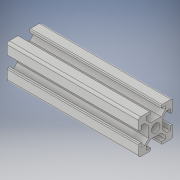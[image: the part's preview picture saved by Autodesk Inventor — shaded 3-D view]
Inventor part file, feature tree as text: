
AUTODESK INVENTOR PART (.ipt)
format: ipt  version: 2019 (Build 230136000, 136)  size: 174,080 bytes
history: native  units: in
note: dims shown in document units (in); Inventor stores cm internally (conversion verified against a paired STEP export)
features: extrude x1, fillet x1, sketch x1
ambient origin geometry x8: Origin, YZ Plane, XZ Plane, XY Plane, X Axis, Y Axis, Z Axis, Center Point
bodies: Solid1 (feature_tree)
feature tree (3):
  extrude  "Extrusion1"  Depth=0.0492in
  fillet  "Fillet1"  [1 undecoded]
  sketch  "Sketch1"  dims[d0=0.1969in d3=0.1417in d4=45.0deg d5=0.122in d7=0.2165in d8=0.063in d11=0.1693in d12=3.0in d13=0.0in d14=0.0492in]
note: 1 required parameter value undecoded (feature->parameter linkage not recoverable at this tier; creation-order binding heuristic only, values carry confidence <= 0.55)
